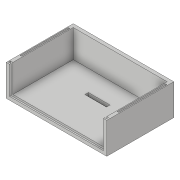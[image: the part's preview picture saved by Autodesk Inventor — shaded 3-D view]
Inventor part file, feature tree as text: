
AUTODESK INVENTOR PART (.ipt)
format: ipt  version: 2018.3 (Build 223284000, 284)  size: 167,936 bytes
history: native  units: in
note: dims shown in document units (in); Inventor stores cm internally (conversion verified against a paired STEP export)
features: extrude x6, sketch x6
ambient origin geometry x8: Origin, YZ Plane, XZ Plane, XY Plane, X Axis, Y Axis, Z Axis, Center Point
bodies: Solid1 (feature_tree)
feature tree (12):
  extrude  "Extrusion1"  Depth=0.647in
  extrude  "Extrusion2"  Depth=0.522in
  extrude  "Extrusion3"  Depth=1.752in
  extrude  "Extrusion4"  Depth=0.0625in
  extrude  "Extrusion5"  Depth=0.408in
  extrude  "Extrusion6"  Depth=0.027in
  sketch  "Sketch1"  dims[d0=1.887in d1=0.647in]
  sketch  "Sketch2"  dims[d2=1.762in d4=0.522in]
  sketch  "Sketch3"  dims[d8=1.0in d9=0.0in d10=1.752in]
  sketch  "Sketch4"  dims[d11=0.0625in d12=0.0625in d13=0.005in]
  sketch  "Sketch5"  dims[d14=0.005in d15=0.408in]
  sketch  "Sketch6"  dims[d16=0.067in d17=0.672in d18=0.672in d22=1.0in d23=0.393in d24=1.0in d25=0.0in d26=0.9in d27=0.05in d28=0.0156in d29=0.0312in d30=0.0156in d31=0.0312in d32=0.05in d33=0.0156in d34=0.125in d35=0.0in d36=0.0625in d37=0.0in d38=0.1955in d39=0.0in d40=0.5625in d41=0.0in d42=0.0355in d43=0.027in]
